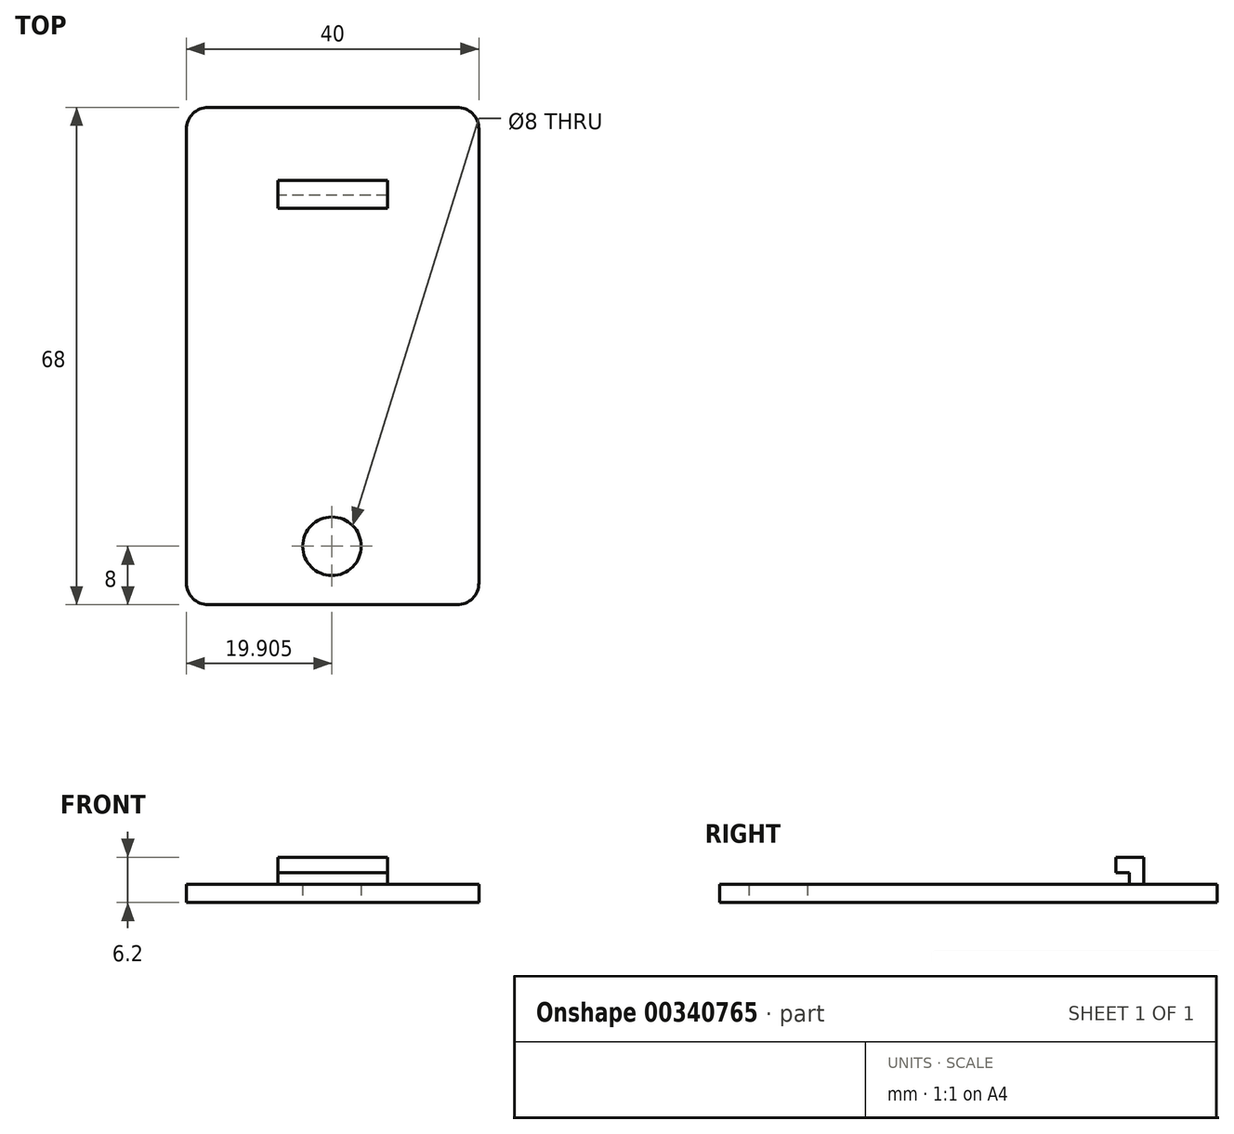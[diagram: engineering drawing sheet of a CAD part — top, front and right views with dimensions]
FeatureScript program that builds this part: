
annotation { "Feature Type Name" : "Feature", "Feature Type Description" : "" }
export const myFeature = defineFeature(function(context is Context, id is Id, definition is map)
    precondition{}
    {
        {
            var Q0;
            Q0=qCreatedBy(makeId("Top.planeOp"),FACE);
            var sketch = newSketch(context, id + "F0", { "sketchPlane" : qUnion([Q0])});
            skLineSegment(sketch, "E0.bottom", {"start": v(-20, 34) * mm, "end": v(20, 34) * mm});
            skLineSegment(sketch, "E0.top", {"start": v(-20, -34) * mm, "end": v(20, -34) * mm});
            skLineSegment(sketch, "E0.left", {"start": v(-20, 34) * mm, "end": v(-20, -34) * mm});
            skLineSegment(sketch, "E0.right", {"start": v(20, 34) * mm, "end": v(20, -34) * mm});
            skPoint(sketch, "E0.middle", {"position": v(0, 0) * mm});
            skLineSegment(sketch, "E1", {"start": v(-39.38, -26) * mm, "end": v(39.18, -26) * mm, "construction": true});
            skCircle(sketch, "E2", {"center": v(-0.1, -26) * mm, "radius": 4 * mm});
            skSolve(sketch);
        }
        {
            var Q0;
            Q0 = qSketchRegion(id + "F0", true);
            extrude(context, id + "F1", {"entities" : qUnion([Q0]), "depth" : 2.5 * mm});
        }
        {
            var Q0;
            Q0=makeQuery(id+"F1.opExtrude","SWEPT_EDGE",EDGE,{"disambiguationData":[OSD([sQuery(id+"F0.wireOp",EDGE,"E0.bottom"),sQuery(id+"F0.wireOp",EDGE,"E0.left")])]});
            var Q1;
            Q1=makeQuery(id+"F1.opExtrude","SWEPT_EDGE",EDGE,{"disambiguationData":[OSD([sQuery(id+"F0.wireOp",EDGE,"E0.bottom"),sQuery(id+"F0.wireOp",EDGE,"E0.right")])]});
            var Q2;
            Q2=makeQuery(id+"F1.opExtrude","SWEPT_EDGE",EDGE,{"disambiguationData":[OSD([sQuery(id+"F0.wireOp",EDGE,"E0.top"),sQuery(id+"F0.wireOp",EDGE,"E0.left")])]});
            var Q3;
            Q3=makeQuery(id+"F1.opExtrude","SWEPT_EDGE",EDGE,{"disambiguationData":[OSD([sQuery(id+"F0.wireOp",EDGE,"E0.top"),sQuery(id+"F0.wireOp",EDGE,"E0.right")])]});
            fillet(context, id + "F2", {"entities" : qUnion([Q0, Q1, Q2, Q3]), "radius" : 3 * mm, "tangentPropagation" : true, "allowEdgeOverflow" : false});
        }
        {
            var Q0;
            Q0=makeQuery(id+"F1.opExtrude","CAP_FACE",FACE,{"disambiguationData":[OSD([sQuery(id+"F0.wireOp",EDGE,"E0.bottom"),sQuery(id+"F0.wireOp",EDGE,"E0.top"),sQuery(id+"F0.wireOp",EDGE,"E0.left"),sQuery(id+"F0.wireOp",EDGE,"E0.right"),sQuery(id+"F0.wireOp",EDGE,"E2")])],"isStart":false});
            var sketch = newSketch(context, id + "F3", { "sketchPlane" : qUnion([Q0])});
            skLineSegment(sketch, "E3", {"start": v(-57.85, 22.1) * mm, "end": v(61.48, 22.1) * mm, "construction": true});
            skLineSegment(sketch, "E4.bottom", {"start": v(7.5, 24) * mm, "end": v(-7.5, 24) * mm});
            skLineSegment(sketch, "E4.top", {"start": v(7.5, 20.2) * mm, "end": v(-7.5, 20.2) * mm});
            skLineSegment(sketch, "E4.left", {"start": v(7.5, 24) * mm, "end": v(7.5, 20.2) * mm});
            skLineSegment(sketch, "E4.right", {"start": v(-7.5, 24) * mm, "end": v(-7.5, 20.2) * mm});
            skPoint(sketch, "E4.middle", {"position": v(0, 22.1) * mm});
            skPoint(sketch, "E4.middle.positionSnap0", {"position": v(0, 34) * mm});
            skPoint(sketch, "E4.centerSnap0", {"position": v(0, 34) * mm});
            skSolve(sketch);
        }
        {
            var Q0;
            Q0=makeQuery(id+"F3.imprint","IMPRINT",FACE,{"disambiguationData":[TD([[makeQuery(id+"F3.imprint","IMPRINT",EDGE,{"derivedFrom":sQuery(id+"F3.wireOp",EDGE,"E4.bottom")}),1.0]])]});
            extrude(context, id + "F4", {"entities" : qUnion([Q0]), "operationType" : NewBodyOperationType.ADD, "depth" : 3.7 * mm});
        }
        {
            var Q0;
            Q0=makeQuery(id+"F4.opExtrude","SWEPT_FACE",FACE,{"disambiguationData":[OSD([sQuery(id+"F3.wireOp",EDGE,"E4.right")])]});
            var sketch = newSketch(context, id + "F5", { "sketchPlane" : qUnion([Q0])});
            skLineSegment(sketch, "E5.bottom", {"start": v(-20.2, 2.5) * mm, "end": v(-22, 2.5) * mm});
            skLineSegment(sketch, "E5.top", {"start": v(-20.2, 4.1) * mm, "end": v(-22, 4.1) * mm});
            skLineSegment(sketch, "E5.left", {"start": v(-20.2, 2.5) * mm, "end": v(-20.2, 4.1) * mm});
            skLineSegment(sketch, "E5.right", {"start": v(-22, 2.5) * mm, "end": v(-22, 4.1) * mm});
            skSolve(sketch);
        }
        {
            var Q0;
            Q0=makeQuery(id+"F5.imprint","IMPRINT",FACE,{"disambiguationData":[TD([[makeQuery(id+"F5.imprint","IMPRINT",EDGE,{"derivedFrom":sQuery(id+"F5.wireOp",EDGE,"E5.bottom")}),1.0]])]});
            extrude(context, id + "F6", {"entities" : qUnion([Q0]), "operationType" : NewBodyOperationType.REMOVE, "oppositeDirection" : true, "depth" : 25 * mm});
        }
    });
